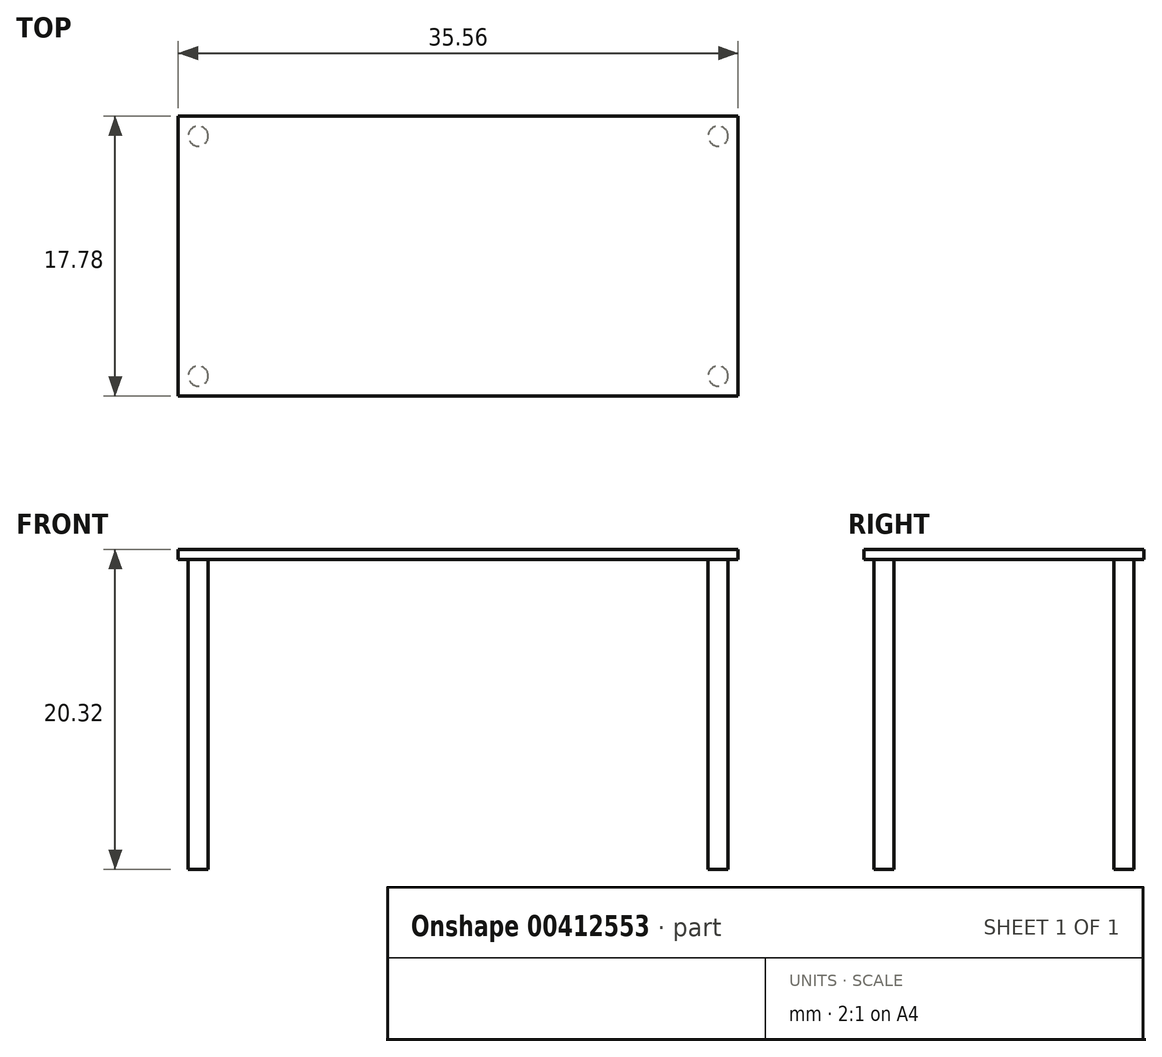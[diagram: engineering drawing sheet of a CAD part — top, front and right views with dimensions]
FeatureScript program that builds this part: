
annotation { "Feature Type Name" : "Feature", "Feature Type Description" : "" }
export const myFeature = defineFeature(function(context is Context, id is Id, definition is map)
    precondition{}
    {
        {
            var Q0;
            Q0=qCreatedBy(makeId("Top.planeOp"),FACE);
            var sketch = newSketch(context, id + "F0", { "sketchPlane" : qUnion([Q0])});
            skLineSegment(sketch, "E0.bottom", {"start": v(0, 0) * mm, "end": v(-35.56, 0) * mm});
            skLineSegment(sketch, "E0.top", {"start": v(0, -17.78) * mm, "end": v(-35.56, -17.78) * mm});
            skLineSegment(sketch, "E0.left", {"start": v(0, 0) * mm, "end": v(0, -17.78) * mm});
            skLineSegment(sketch, "E0.right", {"start": v(-35.56, 0) * mm, "end": v(-35.56, -17.78) * mm});
            skSolve(sketch);
        }
        {
            var Q0;
            Q0 = qSketchRegion(id + "F0", true);
            extrude(context, id + "F1", {"entities" : qUnion([Q0]), "oppositeDirection" : true, "depth" : 0.64 * mm});
        }
        {
            var Q0;
            Q0=qCreatedBy(makeId("Top.planeOp"),FACE);
            var sketch = newSketch(context, id + "F2", { "sketchPlane" : qUnion([Q0])});
            skCircle(sketch, "E1", {"center": v(-34.29, -1.27) * mm, "radius": 0.64 * mm});
            skCircle(sketch, "E2", {"center": v(-34.29, -16.5) * mm, "radius": 0.64 * mm});
            skCircle(sketch, "E3", {"center": v(-1.27, -16.5) * mm, "radius": 0.64 * mm});
            skCircle(sketch, "E4", {"center": v(-1.27, -1.27) * mm, "radius": 0.64 * mm});
            skSolve(sketch);
        }
        {
            var Q0;
            Q0 = qSketchRegion(id + "F2", true);
            extrude(context, id + "F3", {"entities" : qUnion([Q0]), "operationType" : NewBodyOperationType.ADD, "oppositeDirection" : true, "depth" : 20.32 * mm});
        }
    });
